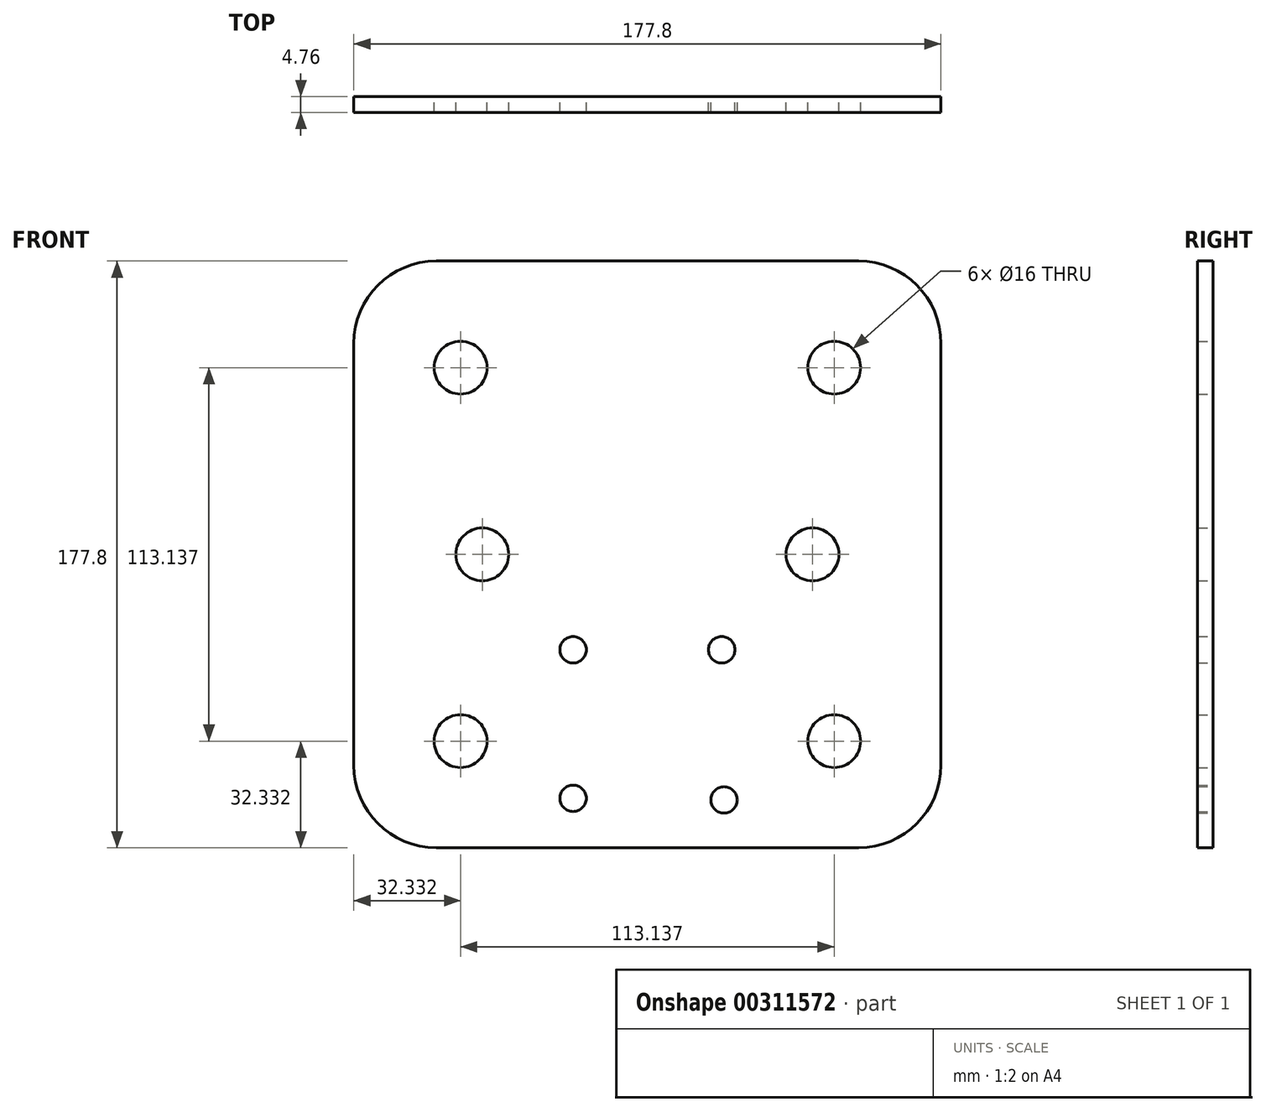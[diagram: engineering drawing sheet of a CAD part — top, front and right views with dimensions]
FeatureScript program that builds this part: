
annotation { "Feature Type Name" : "Feature", "Feature Type Description" : "" }
export const myFeature = defineFeature(function(context is Context, id is Id, definition is map)
    precondition{}
    {
        {
            var Q0;
            Q0=qCreatedBy(makeId("Front.planeOp"),FACE);
            var sketch = newSketch(context, id + "F0", { "sketchPlane" : qUnion([Q0])});
            skLineSegment(sketch, "E0.bottom", {"start": v(63.9, -88.9) * mm, "end": v(-63.9, -88.9) * mm});
            skLineSegment(sketch, "E0.top", {"start": v(63.9, 88.9) * mm, "end": v(-63.9, 88.9) * mm});
            skLineSegment(sketch, "E0.left", {"start": v(88.9, -63.9) * mm, "end": v(88.9, 63.9) * mm});
            skLineSegment(sketch, "E0.right", {"start": v(-88.9, -63.9) * mm, "end": v(-88.9, 63.9) * mm});
            skPoint(sketch, "E0.middle", {"position": v(0, 0) * mm});
            skPoint(sketch, "E1", {"position": v(-56.57, 56.57) * mm});
            skPoint(sketch, "E2", {"position": v(56.57, 56.57) * mm});
            skPoint(sketch, "E3", {"position": v(56.57, -56.57) * mm});
            skPoint(sketch, "E4", {"position": v(-56.57, -56.57) * mm});
            skPoint(sketch, "E5.visualSharp", {"position": v(-88.9, 88.9) * mm});
            skArc(sketch, "E5.filletArc", {"start": v(-63.9, 88.9) * mm, "mid": v(-81.58, 81.58) * mm, "end": v(-88.9, 63.9) * mm});
            skPoint(sketch, "E6.visualSharp", {"position": v(-88.9, -88.9) * mm});
            skArc(sketch, "E6.filletArc", {"start": v(-88.9, -63.9) * mm, "mid": v(-81.58, -81.58) * mm, "end": v(-63.9, -88.9) * mm});
            skPoint(sketch, "E7.visualSharp", {"position": v(88.9, -88.9) * mm});
            skArc(sketch, "E7.filletArc", {"start": v(63.9, -88.9) * mm, "mid": v(81.58, -81.58) * mm, "end": v(88.9, -63.9) * mm});
            skPoint(sketch, "E8.visualSharp", {"position": v(88.9, 88.9) * mm});
            skArc(sketch, "E8.filletArc", {"start": v(88.9, 63.9) * mm, "mid": v(81.58, 81.58) * mm, "end": v(63.9, 88.9) * mm});
            skCircle(sketch, "E9", {"center": v(-56.57, 56.57) * mm, "radius": 8 * mm});
            skCircle(sketch, "E10", {"center": v(56.57, 56.57) * mm, "radius": 8 * mm});
            skCircle(sketch, "E11", {"center": v(-56.57, -56.57) * mm, "radius": 8 * mm});
            skCircle(sketch, "E12", {"center": v(56.57, -56.57) * mm, "radius": 8 * mm});
            skPoint(sketch, "E13", {"position": v(0, -73.9) * mm});
            skPoint(sketch, "E13.positionSnap0", {"position": v(0, -88.9) * mm});
            skPoint(sketch, "E14", {"position": v(-22.5, -73.9) * mm});
            skPoint(sketch, "E15", {"position": v(22.5, -73.9) * mm});
            skPoint(sketch, "E16", {"position": v(-22.5, -28.9) * mm});
            skPoint(sketch, "E17", {"position": v(22.5, -28.9) * mm});
            skCircle(sketch, "E18", {"center": v(-22.5, -28.9) * mm, "radius": 4 * mm});
            skCircle(sketch, "E19", {"center": v(22.5, -28.9) * mm, "radius": 4 * mm});
            skCircle(sketch, "E20", {"center": v(-22.5, -73.9) * mm, "radius": 4 * mm});
            skCircle(sketch, "E21", {"center": v(23.2, -74.4) * mm, "radius": 4 * mm});
            skPoint(sketch, "E22", {"position": v(-50, 0) * mm});
            skPoint(sketch, "E23", {"position": v(50, 0) * mm});
            skCircle(sketch, "E24", {"center": v(-50, 0) * mm, "radius": 8 * mm});
            skCircle(sketch, "E25", {"center": v(50, 0) * mm, "radius": 8 * mm});
            skSolve(sketch);
        }
        {
            var Q0;
            Q0=makeQuery(id+"F0.imprint","IMPRINT",FACE,{"disambiguationData":[TD([[makeQuery(id+"F0.imprint","IMPRINT",EDGE,{"derivedFrom":sQuery(id+"F0.wireOp",EDGE,"E0.bottom")}),-1.0]])]});
            extrude(context, id + "F1", {"entities" : qUnion([Q0]), "depth" : 4.76 * mm});
        }
    });
